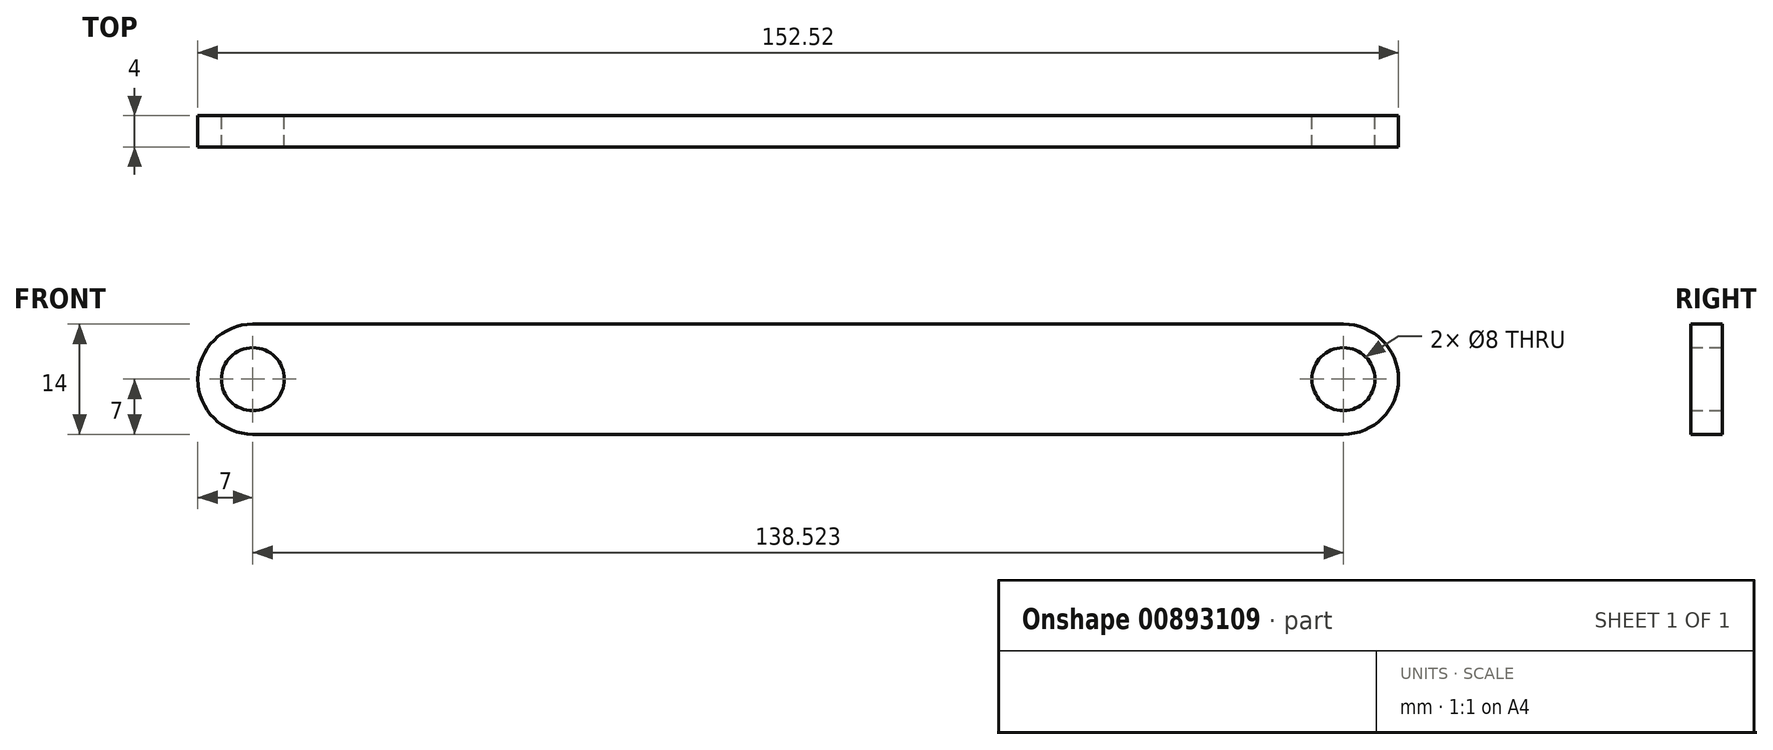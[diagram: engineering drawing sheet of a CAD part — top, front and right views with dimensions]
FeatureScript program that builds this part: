
annotation { "Feature Type Name" : "Feature", "Feature Type Description" : "" }
export const myFeature = defineFeature(function(context is Context, id is Id, definition is map)
    precondition{}
    {
        {
            assignVariable(context, id + "F0", {"name" : "Thickness", "anyValue" : 4});
        }
        {
            var Q0;
            Q0=qCreatedBy(makeId("Front.planeOp"),FACE);
            var sketch = newSketch(context, id + "F1", { "sketchPlane" : qUnion([Q0])});
            skCircle(sketch, "E0", {"center": v(0, 0) * mm, "radius": 4 * mm});
            skCircle(sketch, "E1", {"center": v(138.52, 0) * mm, "radius": 4 * mm});
            skArc(sketch, "E2", {"start": v(138.52, -7) * mm, "mid": v(145.52, 0) * mm, "end": v(138.52, 7) * mm});
            skArc(sketch, "E3", {"start": v(0, 7) * mm, "mid": v(-7, 0) * mm, "end": v(0, -7) * mm});
            skLineSegment(sketch, "E4", {"start": v(0, 7) * mm, "end": v(138.52, 7) * mm});
            skLineSegment(sketch, "E5", {"start": v(0, -7) * mm, "end": v(138.52, -7) * mm});
            skSolve(sketch);
        }
        {
            var Q0;
            Q0=makeQuery(id+"F1.imprint","IMPRINT",FACE,{"disambiguationData":[TD([[makeQuery(id+"F1.imprint","IMPRINT",EDGE,{"derivedFrom":sQuery(id+"F1.wireOp",EDGE,"E0")}),-1.0]])]});
            extrude(context, id + "F2", {"entities" : qUnion([Q0]), "depth" : (getVariable(context, 'Thickness')) * mm, "offsetDistance" : 25 * mm});
        }
    });
